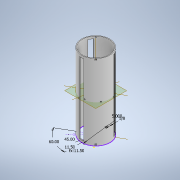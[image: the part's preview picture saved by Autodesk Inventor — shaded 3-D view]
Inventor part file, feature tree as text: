
AUTODESK INVENTOR PART (.ipt)
format: ipt  version: 2021 (Build 250183000, 183)  size: 260,608 bytes
history: native  units: in
note: dims shown in document units (in); Inventor stores cm internally (conversion verified against a paired STEP export)
features: other x26, plane x5, hole x5, pattern_circular x4, sketch x4, extrude x2
ambient origin geometry x8: Origin, YZ Plane, XZ Plane, XY Plane, X Axis, Y Axis, Z Axis, Center Point
bodies: Solid1 (feature_tree)
feature tree (46):
  extrude  "Extrusion1"  Depth=0.3937in
  plane  "Work Plane1"
  extrude  "Extrusion2"  Depth=0.3937in TaperAngle=0.0deg
  pattern_circular  "Circular Pattern1"  Count=3 Angle=360.0deg
  other  "Work Axis1"
  other  "Work Axis2"
  other  "Work Axis3"
  other  "Work Axis4"
  other  "Work Point1"
  other  "Work Point2"
  other  "Work Point3"
  other  "Central Plane"
  other  "Work Point4"
  other  "Work Axis6"
  other  "Work Axis7"
  other  "Offset Plane A"
  other  "Work Point5"
  other  "Work Point6"
  other  "Work Axis8"
  other  "Work Axis9"
  other  "Work Point7"
  other  "Work Point8"
  plane  "Work Plane5"
  plane  "Work Plane6"
  hole  "Hole1"  [1 undecoded]
  hole  "Hole2"  [1 undecoded]
  pattern_circular  "Circular Pattern3"  [2 undecoded]
  sketch  "Sketch5"  dims[d13=0.079in d14=-6.6929in]
  plane  "Work Plane7"
  sketch  "Sketch6"  dims[d15=0.079in d16=0.1574in d17=-0.1574in d48=1.0in d49=1.0in d29=0.096in d30=0.75in d31=0.185in d32=0.25in d33=0.5635in d34=1.0in d35=0.0in d52=1.0in d53=1.0in d38=0.096in d39=0.75in d40=0.185in d41=0.25in d42=0.5635in d43=1.0in d44=0.8108in d45=1.1811in d46=360.0deg d51=0.38in d54=0.177in d55=0.328in d56=0.332in d57=0.25in d58=0.5635in d59=0.484in d60=0.8108in d64=0.19in d65=0.177in d66=0.3229in d67=0.332in d68=0.25in d69=0.5635in d70=0.484in d71=0.8108in d72=1.5748in d73=360.0deg d75=60.0deg d76=1.0in d77=1.0in d78=0.129in d79=0.3229in d80=0.225in d81=0.25in d82=0.5635in d83=0.484in d84=0.8108in d85=1.1811in d86=360.0deg d61=0.75in d62=0.8108in d63=0.0625in]
  hole  "Hole3"  [1 undecoded]
  other  "Work Axis10"
  hole  "Hole4"  [1 undecoded]
  pattern_circular  "Circular Pattern5"  [2 undecoded]
  plane  "Work Plane12"
  hole  "Hole5"  [1 undecoded]
  pattern_circular  "Circular Pattern6"  Angle=60.0deg  [1 undecoded]
  sketch  "Sketch1"  dims[d3=0.0in d5=0.3937in]
  sketch  "Sketch2"  dims[d7=0.3937in d8=0.5in d9=0.0in d10=1.1811in d11=360.0deg]
  other  "Work Axis5"
  other  "Offset Plane B"
  other  "Work Axis11"
  other  "Work Axis12"
  other  "Work Point9"
  other  "Work Axis13"
  other  "Work Point10"
note: 10 required parameter values undecoded (feature->parameter linkage not recoverable at this tier; creation-order binding heuristic only, values carry confidence <= 0.55)
